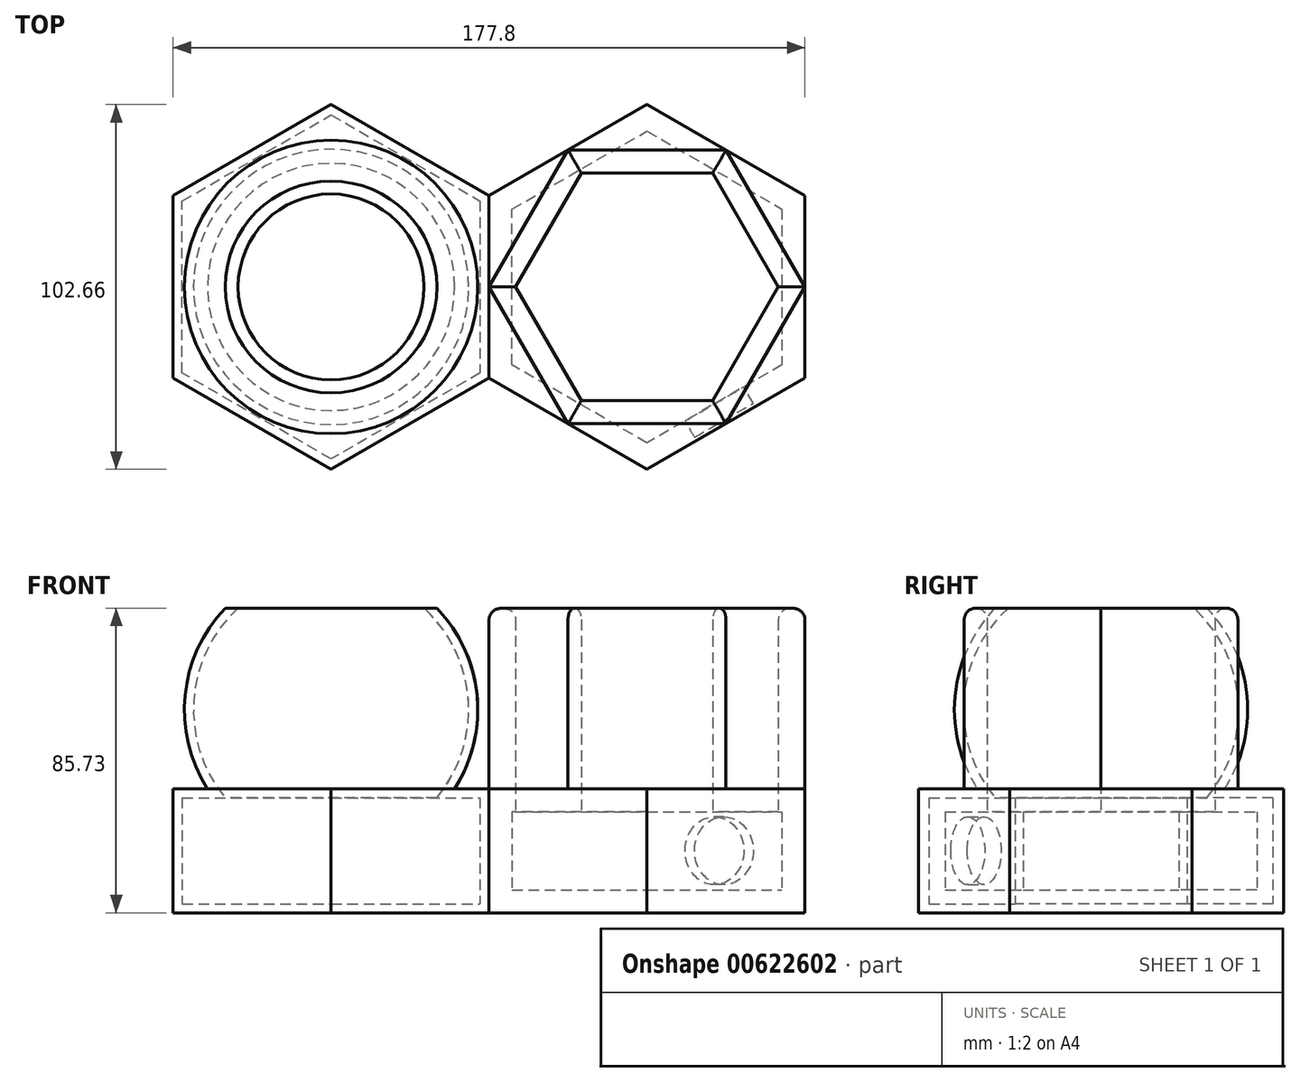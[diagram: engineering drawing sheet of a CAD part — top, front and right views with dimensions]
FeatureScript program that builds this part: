
annotation { "Feature Type Name" : "Feature", "Feature Type Description" : "" }
export const myFeature = defineFeature(function(context is Context, id is Id, definition is map)
    precondition{}
    {
        {
            var Q0;
            Q0=qCreatedBy(makeId("Top.planeOp"),FACE);
            var sketch = newSketch(context, id + "F0", { "sketchPlane" : qUnion([Q0])});
            skCircle(sketch, "E0.cCircle", {"center": v(0, 0) * mm, "radius": 44.45 * mm, "construction": true});
            skLineSegment(sketch, "E0.0", {"start": v(0, 51.33) * mm, "end": v(44.45, 25.66) * mm});
            skLineSegment(sketch, "E0.1", {"start": v(44.45, 25.66) * mm, "end": v(44.45, -25.66) * mm});
            skLineSegment(sketch, "E0.2", {"start": v(44.45, -25.66) * mm, "end": v(0, -51.33) * mm});
            skLineSegment(sketch, "E0.3", {"start": v(0, -51.33) * mm, "end": v(-44.45, -25.66) * mm});
            skLineSegment(sketch, "E0.4", {"start": v(-44.45, -25.66) * mm, "end": v(-44.45, 25.66) * mm});
            skLineSegment(sketch, "E0.5", {"start": v(-44.45, 25.66) * mm, "end": v(0, 51.33) * mm});
            skPoint(sketch, "E0.0.midPoint", {"position": v(22.22, 38.5) * mm});
            skSolve(sketch);
        }
        {
            var Q0;
            Q0 = qSketchRegion(id + "F0", true);
            extrude(context, id + "F1", {"entities" : qUnion([Q0]), "depth" : 34.92 * mm, "offsetDistance" : 25.4 * mm});
        }
        {
            var Q0;
            Q0=makeQuery(id+"F1.opExtrude","CAP_FACE",FACE,{"disambiguationData":[OSD([sQuery(id+"F0.wireOp",EDGE,"E0.0"),sQuery(id+"F0.wireOp",EDGE,"E0.1"),sQuery(id+"F0.wireOp",EDGE,"E0.2"),sQuery(id+"F0.wireOp",EDGE,"E0.3"),sQuery(id+"F0.wireOp",EDGE,"E0.4"),sQuery(id+"F0.wireOp",EDGE,"E0.5")])],"isStart":false});
            var sketch = newSketch(context, id + "F2", { "sketchPlane" : qUnion([Q0])});
            skCircle(sketch, "E1.cCircle", {"center": v(0, 0) * mm, "radius": 38.5 * mm, "construction": true});
            skLineSegment(sketch, "E1.0", {"start": v(22.23, 38.5) * mm, "end": v(44.45, 0) * mm});
            skLineSegment(sketch, "E1.1", {"start": v(44.45, 0) * mm, "end": v(22.23, -38.5) * mm});
            skLineSegment(sketch, "E1.2", {"start": v(22.23, -38.5) * mm, "end": v(-22.22, -38.5) * mm});
            skLineSegment(sketch, "E1.3", {"start": v(-22.22, -38.5) * mm, "end": v(-44.45, 0) * mm});
            skLineSegment(sketch, "E1.4", {"start": v(-44.45, 0) * mm, "end": v(-22.22, 38.5) * mm});
            skLineSegment(sketch, "E1.5", {"start": v(-22.22, 38.5) * mm, "end": v(22.23, 38.5) * mm});
            skPoint(sketch, "E1.0.midPoint", {"position": v(33.34, 19.25) * mm});
            skLineSegment(sketch, "E2", {"start": v(0, 0) * mm, "end": v(22.23, 38.5) * mm, "construction": true});
            skSolve(sketch);
        }
        {
            var Q0;
            Q0 = qSketchRegion(id + "F2", true);
            extrude(context, id + "F3", {"entities" : qUnion([Q0]), "operationType" : NewBodyOperationType.ADD, "depth" : 50.8 * mm, "offsetDistance" : 25.4 * mm});
        }
        {
            var Q0;
            Q0=makeQuery(id+"F3.opExtrude","CAP_FACE",FACE,{"disambiguationData":[OSD([sQuery(id+"F2.wireOp",EDGE,"E1.0"),sQuery(id+"F2.wireOp",EDGE,"E1.1"),sQuery(id+"F2.wireOp",EDGE,"E1.2"),sQuery(id+"F2.wireOp",EDGE,"E1.3"),sQuery(id+"F2.wireOp",EDGE,"E1.4"),sQuery(id+"F2.wireOp",EDGE,"E1.5")])],"isStart":false});
            shell(context, id + "F4", {"entities" : qUnion([Q0]), "thickness" : 6.48 * mm});
        }
        {
            var Q0;
            Q0=makeQuery(id+"F3.opExtrude","CAP_FACE",FACE,{"disambiguationData":[OSD([sQuery(id+"F2.wireOp",EDGE,"E1.0"),sQuery(id+"F2.wireOp",EDGE,"E1.1"),sQuery(id+"F2.wireOp",EDGE,"E1.2"),sQuery(id+"F2.wireOp",EDGE,"E1.3"),sQuery(id+"F2.wireOp",EDGE,"E1.4"),sQuery(id+"F2.wireOp",EDGE,"E1.5")])],"isStart":false});
            fillet(context, id + "F5", {"entities" : qUnion([Q0]), "radius" : 3.24 * mm, "tangentPropagation" : true, "allowEdgeOverflow" : false});
        }
        {
            var Q0;
            Q0=makeQuery(id+"F4.opShell","OFFSET_FACE",FACE,{"disambiguationData":[OSD([sQuery(id+"F0.wireOp",EDGE,"E0.2")])]});
            var sketch = newSketch(context, id + "F6", { "sketchPlane" : qUnion([Q0])});
            skCircle(sketch, "E3", {"center": v(0, 17.46) * mm, "radius": 9.55 * mm});
            skSolve(sketch);
        }
        {
            var Q0;
            Q0 = qSketchRegion(id + "F6", true);
            extrude(context, id + "F7", {"entities" : qUnion([Q0]), "operationType" : NewBodyOperationType.REMOVE, "oppositeDirection" : true, "depth" : 5.33 * mm, "offsetDistance" : 25.4 * mm});
        }
        {
            var Q0;
            Q0=qCreatedBy(makeId("Top.planeOp"),FACE);
            var sketch = newSketch(context, id + "F8", { "sketchPlane" : qUnion([Q0])});
            skCircle(sketch, "E4.cCircle", {"center": v(-88.9, 0) * mm, "radius": 44.45 * mm, "construction": true});
            skLineSegment(sketch, "E4.0", {"start": v(-44.45, 25.66) * mm, "end": v(-44.45, -25.66) * mm});
            skLineSegment(sketch, "E4.1", {"start": v(-44.45, -25.66) * mm, "end": v(-88.9, -51.33) * mm});
            skLineSegment(sketch, "E4.2", {"start": v(-88.9, -51.33) * mm, "end": v(-133.35, -25.66) * mm});
            skLineSegment(sketch, "E4.3", {"start": v(-133.35, -25.66) * mm, "end": v(-133.35, 25.66) * mm});
            skLineSegment(sketch, "E4.4", {"start": v(-133.35, 25.66) * mm, "end": v(-88.9, 51.33) * mm});
            skLineSegment(sketch, "E4.5", {"start": v(-88.9, 51.33) * mm, "end": v(-44.45, 25.66) * mm});
            skPoint(sketch, "E4.0.midPoint", {"position": v(-44.45, 0) * mm});
            skSolve(sketch);
        }
        {
            var Q0;
            Q0 = qSketchRegion(id + "F8", true);
            extrude(context, id + "F9", {"entities" : qUnion([Q0]), "depth" : 34.92 * mm, "offsetDistance" : 25.4 * mm});
        }
        {
            var Q0;
            Q0=qCreatedBy(makeId("Front.planeOp"),FACE);
            var sketch = newSketch(context, id + "F10", { "sketchPlane" : qUnion([Q0])});
            skCircle(sketch, "E5", {"center": v(-88.9, 57.15) * mm, "radius": 41.28 * mm});
            skLineSegment(sketch, "E6", {"start": v(-88.9, 98.43) * mm, "end": v(-88.9, 15.88) * mm});
            skSolve(sketch);
        }
        {
            var Q0;
            Q0=makeQuery(id+"F9.opExtrude","CAP_FACE",FACE,{"disambiguationData":[OSD([sQuery(id+"F8.wireOp",EDGE,"E4.0"),sQuery(id+"F8.wireOp",EDGE,"E4.1"),sQuery(id+"F8.wireOp",EDGE,"E4.2"),sQuery(id+"F8.wireOp",EDGE,"E4.3"),sQuery(id+"F8.wireOp",EDGE,"E4.4"),sQuery(id+"F8.wireOp",EDGE,"E4.5")])],"isStart":false});
            cPlane(context, id + "F11", {"entities" : qUnion([Q0]), "cplaneType" : CPlaneType.OFFSET, "offset" : 50.8 * mm, "width" : 152.4 * mm, "height" : 152.4 * mm});
        }
        {
            var Q0;
            {var subQ0=sQuery(id+"F10.wireOp",EDGE,"E6");Q0=makeQuery(id+"F10.imprint","IMPRINT",FACE,{"disambiguationData":[TD([[makeQuery(id+"F10.imprint","IMPRINT",EDGE,{"derivedFrom":subQ0}),1.0]])]});}
            var Q1;
            Q1=sQuery(id+"F10.wireOp",EDGE,"E6");
            revolve(context, id + "F12", {"operationType" : NewBodyOperationType.ADD, "entities" : qUnion([Q0]), "axis" : qUnion([Q1]), "revolveType" : RevolveType.FULL});
        }
        {
            var Q0;
            Q0=qCreatedBy(makeId("Front.planeOp"),FACE);
            var sketch = newSketch(context, id + "F13", { "sketchPlane" : qUnion([Q0])});
            skCircle(sketch, "E7", {"center": v(-88.9, 98.43) * mm, "radius": 15.88 * mm});
            skLineSegment(sketch, "E8", {"start": v(-133.8, 98.43) * mm, "end": v(-58.07, 98.43) * mm, "construction": true});
            skLineSegment(sketch, "E9", {"start": v(-88.9, 82.55) * mm, "end": v(-88.9, 114.3) * mm});
            skSolve(sketch);
        }
        {
            var Q0;
            {var subQ0=sQuery(id+"F13.wireOp",EDGE,"E9");Q0=makeQuery(id+"F13.imprint","IMPRINT",FACE,{"disambiguationData":[TD([[makeQuery(id+"F13.imprint","IMPRINT",EDGE,{"derivedFrom":subQ0}),-1.0]])]});}
            var Q1;
            Q1=sQuery(id+"F13.wireOp",EDGE,"E9");
            revolve(context, id + "F14", {"operationType" : NewBodyOperationType.REMOVE, "entities" : qUnion([Q0]), "axis" : qUnion([Q1]), "revolveType" : RevolveType.FULL, "oppositeDirection" : true});
        }
        {
            var Q0;
            Q0=makeQuery(id+"F14.boolean.opBoolean","COPY",FACE,{"derivedFrom":makeQuery(id+"F14.opRevolve","SWEPT_FACE",FACE,{"disambiguationData":[OSD([sQuery(id+"F13.wireOp",EDGE,"E7")])]})});
            shell(context, id + "F15", {"entities" : qUnion([Q0]), "thickness" : 2.54 * mm});
        }
        {
            var Q0;
            Q0=qCreatedBy(id+"F11.planeOp",FACE);
            var sketch = newSketch(context, id + "F16", { "sketchPlane" : qUnion([Q0])});
            skLineSegment(sketch, "E10.bottom", {"start": v(-138.2, 45.1) * mm, "end": v(-47.44, 45.1) * mm});
            skLineSegment(sketch, "E10.top", {"start": v(-138.2, -75.38) * mm, "end": v(-47.44, -75.38) * mm});
            skLineSegment(sketch, "E10.left", {"start": v(-138.2, 45.1) * mm, "end": v(-138.2, -75.38) * mm});
            skLineSegment(sketch, "E10.right", {"start": v(-47.44, 45.1) * mm, "end": v(-47.44, -75.38) * mm});
            skSolve(sketch);
        }
        {
            var Q0;
            Q0 = qSketchRegion(id + "F16", true);
            extrude(context, id + "F17", {"entities" : qUnion([Q0]), "operationType" : NewBodyOperationType.REMOVE, "depth" : 25.4 * mm, "offsetDistance" : 25.4 * mm});
        }
    });
